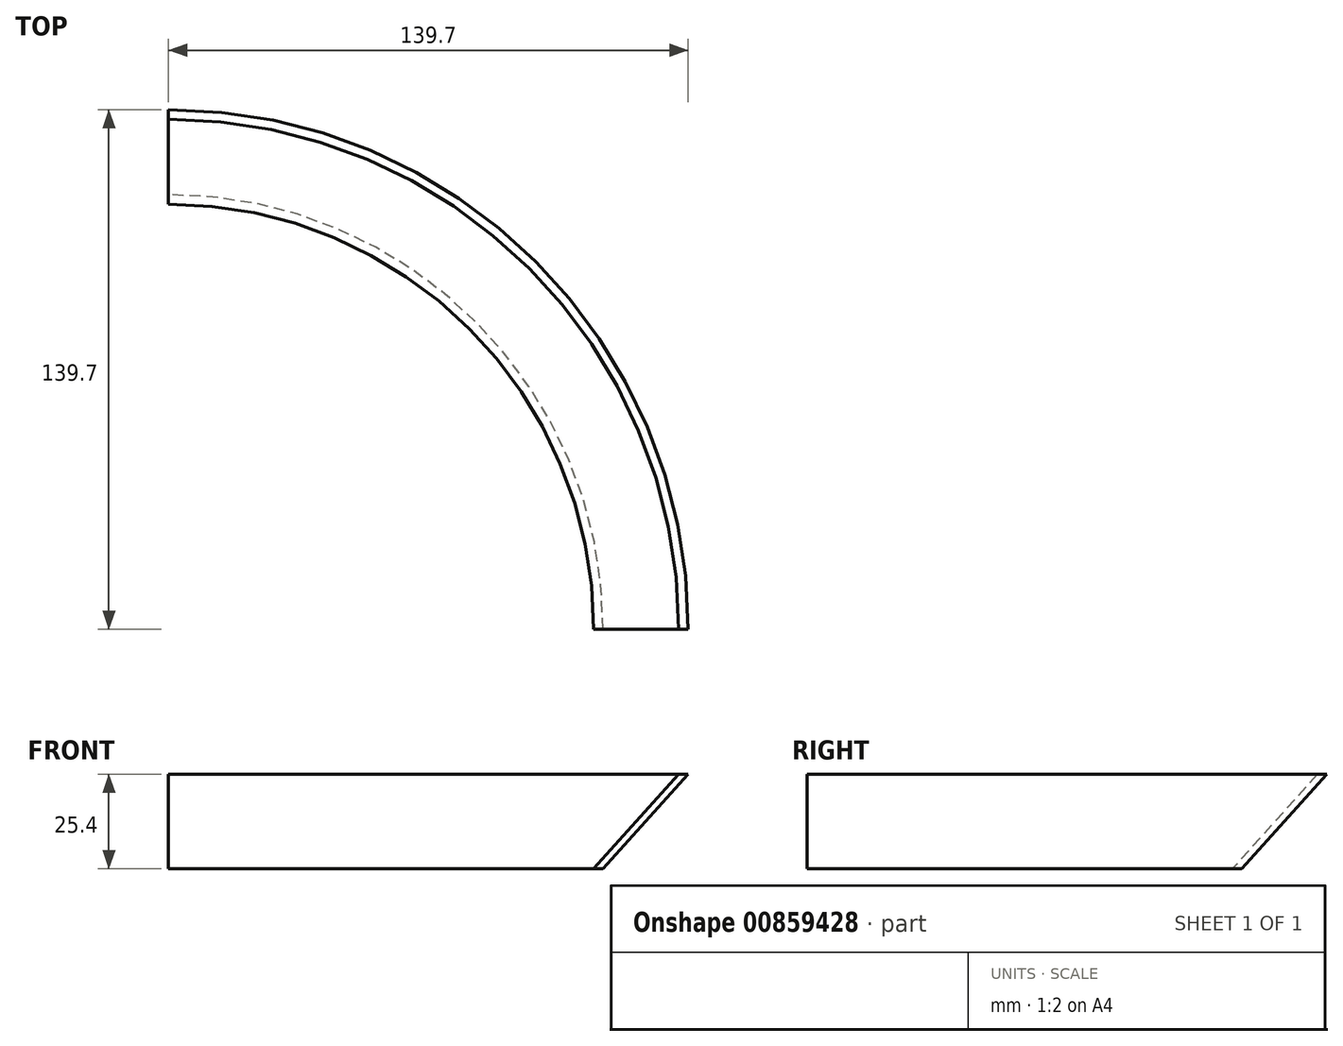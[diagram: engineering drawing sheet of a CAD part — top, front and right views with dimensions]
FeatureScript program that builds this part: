
annotation { "Feature Type Name" : "Feature", "Feature Type Description" : "" }
export const myFeature = defineFeature(function(context is Context, id is Id, definition is map)
    precondition{}
    {
        {
            var Q0;
            Q0=qCreatedBy(makeId("Front.planeOp"),FACE);
            var sketch = newSketch(context, id + "F0", { "sketchPlane" : qUnion([Q0])});
            skLineSegment(sketch, "E0", {"start": v(116.84, 0) * mm, "end": v(139.7, 25.4) * mm});
            skLineSegment(sketch, "E1", {"start": v(139.7, 25.4) * mm, "end": v(137.16, 25.4) * mm});
            skLineSegment(sketch, "E2", {"start": v(137.16, 25.4) * mm, "end": v(114.3, 0) * mm});
            skLineSegment(sketch, "E3", {"start": v(114.3, 0) * mm, "end": v(116.84, 0) * mm});
            skLineSegment(sketch, "E4", {"start": v(0, 14.97) * mm, "end": v(0, 0) * mm});
            skLineSegment(sketch, "E5", {"start": v(0, 0) * mm, "end": v(0, 25.4) * mm});
            skLineSegment(sketch, "E6", {"start": v(0, 25.4) * mm, "end": v(139.7, 25.4) * mm});
            skSolve(sketch);
        }
        {
            var Q0;
            {var subQ0=sQuery(id+"F0.wireOp",EDGE,"E0");Q0=makeQuery(id+"F0.imprint","IMPRINT",FACE,{"disambiguationData":[TD([[makeQuery(id+"F0.imprint","IMPRINT",EDGE,{"derivedFrom":subQ0}),1.0]])]});}
            var Q1;
            Q1=sQuery(id+"F0.wireOp",EDGE,"E5");
            revolve(context, id + "F1", {"surfaceOperationType" : NewSurfaceOperationType.NEW, "entities" : qUnion([Q0]), "axis" : qUnion([Q1]), "revolveType" : RevolveType.ONE_DIRECTION, "angle" : 90 * degree});
        }
    });
